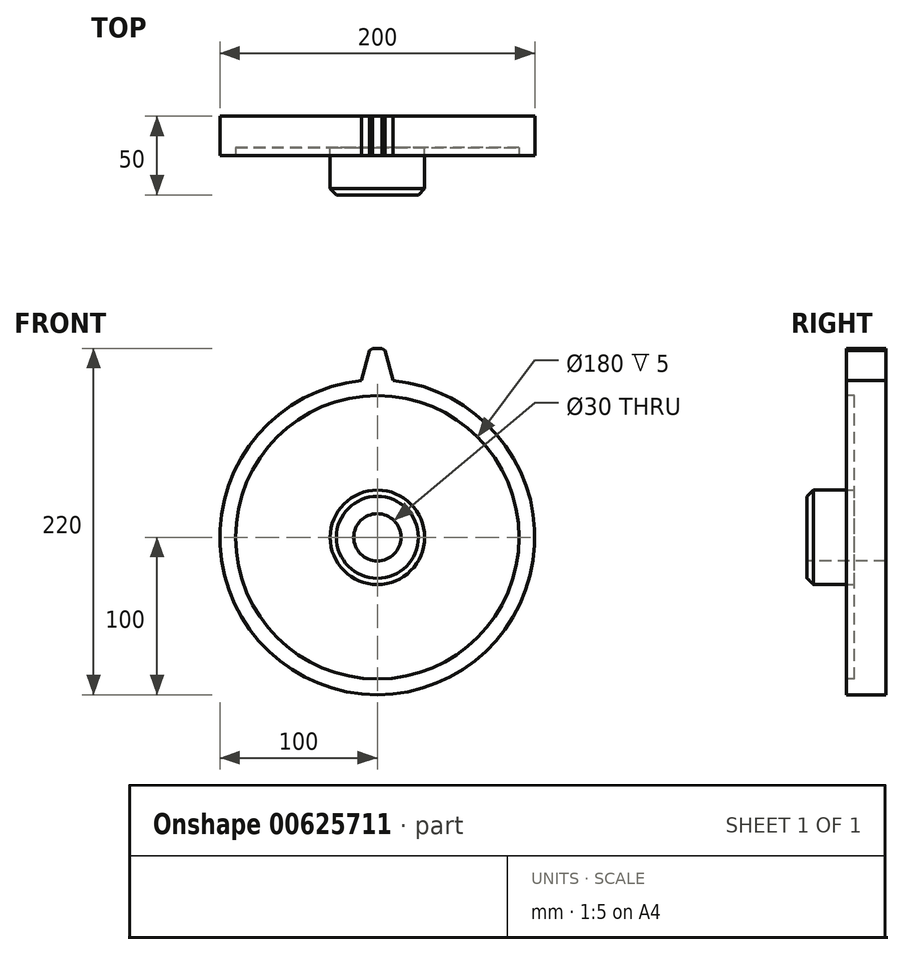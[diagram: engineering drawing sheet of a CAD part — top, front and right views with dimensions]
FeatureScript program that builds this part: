
annotation { "Feature Type Name" : "Feature", "Feature Type Description" : "" }
export const myFeature = defineFeature(function(context is Context, id is Id, definition is map)
    precondition{}
    {
        {
            var Q0;
            Q0=qCreatedBy(makeId("Front.planeOp"),FACE);
            var sketch = newSketch(context, id + "F0", { "sketchPlane" : qUnion([Q0])});
            skCircle(sketch, "E0", {"center": v(0, 0) * mm, "radius": 100 * mm});
            skSolve(sketch);
        }
        {
            var Q0;
            Q0=makeQuery(id+"F0.imprint","IMPRINT",FACE,{"disambiguationData":[TD([[makeQuery(id+"F0.imprint","IMPRINT",EDGE,{"derivedFrom":sQuery(id+"F0.wireOp",EDGE,"E0")}),1.0]])]});
            extrude(context, id + "F1", {"entities" : qUnion([Q0]), "depth" : 25 * mm, "offsetDistance" : 25 * mm});
        }
        {
            var Q0;
            Q0=makeQuery(id+"F1.opExtrude","CAP_FACE",FACE,{"disambiguationData":[OSD([sQuery(id+"F0.wireOp",EDGE,"E0")])],"isStart":false});
            var sketch = newSketch(context, id + "F2", { "sketchPlane" : qUnion([Q0])});
            skLineSegment(sketch, "E1", {"start": v(-10, 99.5) * mm, "end": v(10, 99.5) * mm});
            skLineSegment(sketch, "E2", {"start": v(10, 99.5) * mm, "end": v(4.5, 120) * mm});
            skLineSegment(sketch, "E3", {"start": v(4.5, 120) * mm, "end": v(-4.5, 120) * mm});
            skLineSegment(sketch, "E4", {"start": v(-4.5, 120) * mm, "end": v(-10, 99.5) * mm});
            skSolve(sketch);
        }
        {
            var Q0;
            {var subQ0=sQuery(id+"F2.wireOp",EDGE,"E2");Q0=makeQuery(id+"F2.imprint","IMPRINT",FACE,{"disambiguationData":[TD([[makeQuery(id+"F2.imprint","IMPRINT",EDGE,{"derivedFrom":subQ0}),1.0]])]});}
            var Q1;
            Q1=makeQuery(id+"F1.opExtrude","CAP_FACE",FACE,{"disambiguationData":[OSD([sQuery(id+"F0.wireOp",EDGE,"E0")])],"isStart":true});
            extrude(context, id + "F3", {"entities" : qUnion([Q0]), "operationType" : NewBodyOperationType.ADD, "endBound" : BoundingType.UP_TO_SURFACE, "oppositeDirection" : true, "depth" : 25 * mm, "endBoundEntityFace" : qUnion([Q1]), "offsetDistance" : 25 * mm});
        }
        {
            var Q0;
            Q0=makeQuery(id+"F3.opExtrude","SWEPT_EDGE",EDGE,{"disambiguationData":[OSD([sQuery(id+"F0.wireOp",EDGE,"E0"),sQuery(id+"F2.wireOp",EDGE,"E1"),sQuery(id+"F2.wireOp",EDGE,"E2")])]});
            var Q1;
            Q1=makeQuery(id+"F3.opExtrude","SWEPT_EDGE",EDGE,{"disambiguationData":[OSD([sQuery(id+"F0.wireOp",EDGE,"E0"),sQuery(id+"F2.wireOp",EDGE,"E1"),sQuery(id+"F2.wireOp",EDGE,"E4")])]});
            fillet(context, id + "F4", {"entities" : qUnion([Q0, Q1]), "radius" : 5 * mm, "tangentPropagation" : true, "allowEdgeOverflow" : false});
        }
        {
            var Q0;
            Q0=makeQuery(id+"F3.opExtrude","SWEPT_EDGE",EDGE,{"disambiguationData":[OSD([sQuery(id+"F2.wireOp",EDGE,"E2"),sQuery(id+"F2.wireOp",EDGE,"E3")])]});
            var Q1;
            Q1=makeQuery(id+"F3.opExtrude","SWEPT_EDGE",EDGE,{"disambiguationData":[OSD([sQuery(id+"F2.wireOp",EDGE,"E3"),sQuery(id+"F2.wireOp",EDGE,"E4")])]});
            chamfer(context, id + "F5", {"entities" : qUnion([Q0, Q1]), "width" : 2 * mm, "tangentPropagation" : true});
        }
        {
            var Q0;
            {var subQ0=sQuery(id+"F2.wireOp",EDGE,"E4");var subQ1=sQuery(id+"F2.wireOp",EDGE,"E3");var subQ2=sQuery(id+"F2.wireOp",EDGE,"E2");var subQ3=sQuery(id+"F0.wireOp",EDGE,"E0");Q0=makeQuery(id+"FVngeMlJqadk3JX_1.19.F3.boolean.opBoolean","MERGE",FACE,{"derivedFrom":[makeQuery(id+"FVngeMlJqadk3JX_1.18.F3.boolean.opBoolean","MERGE",FACE,{"derivedFrom":[makeQuery(id+"FVngeMlJqadk3JX_1.17.F3.boolean.opBoolean","MERGE",FACE,{"derivedFrom":[makeQuery(id+"FVngeMlJqadk3JX_1.16.F3.boolean.opBoolean","MERGE",FACE,{"derivedFrom":[makeQuery(id+"FVngeMlJqadk3JX_1.15.F3.boolean.opBoolean","MERGE",FACE,{"derivedFrom":[makeQuery(id+"FVngeMlJqadk3JX_1.14.F3.boolean.opBoolean","MERGE",FACE,{"derivedFrom":[makeQuery(id+"FVngeMlJqadk3JX_1.13.F3.boolean.opBoolean","MERGE",FACE,{"derivedFrom":[makeQuery(id+"FVngeMlJqadk3JX_1.12.F3.boolean.opBoolean","MERGE",FACE,{"derivedFrom":[makeQuery(id+"FVngeMlJqadk3JX_1.11.F3.boolean.opBoolean","MERGE",FACE,{"derivedFrom":[makeQuery(id+"FVngeMlJqadk3JX_1.10.F3.boolean.opBoolean","MERGE",FACE,{"derivedFrom":[makeQuery(id+"FVngeMlJqadk3JX_1.9.F3.boolean.opBoolean","MERGE",FACE,{"derivedFrom":[makeQuery(id+"FVngeMlJqadk3JX_1.8.F3.boolean.opBoolean","MERGE",FACE,{"derivedFrom":[makeQuery(id+"FVngeMlJqadk3JX_1.7.F3.boolean.opBoolean","MERGE",FACE,{"derivedFrom":[makeQuery(id+"FVngeMlJqadk3JX_1.6.F3.boolean.opBoolean","MERGE",FACE,{"derivedFrom":[makeQuery(id+"FVngeMlJqadk3JX_1.5.F3.boolean.opBoolean","MERGE",FACE,{"derivedFrom":[makeQuery(id+"FVngeMlJqadk3JX_1.4.F3.boolean.opBoolean","MERGE",FACE,{"derivedFrom":[makeQuery(id+"FVngeMlJqadk3JX_1.3.F3.boolean.opBoolean","MERGE",FACE,{"derivedFrom":[makeQuery(id+"FVngeMlJqadk3JX_1.2.F3.boolean.opBoolean","MERGE",FACE,{"derivedFrom":[makeQuery(id+"FVngeMlJqadk3JX_1.1.F3.boolean.opBoolean","MERGE",FACE,{"derivedFrom":[makeQuery(id+"F3.boolean.opBoolean","MERGE",FACE,{"derivedFrom":[makeQuery(id+"F1.opExtrude","CAP_FACE",FACE,{"disambiguationData":[OSD([subQ3])],"isStart":false}),makeQuery(id+"F3.opExtrude","CAP_FACE",FACE,{"disambiguationData":[OSD([subQ3,subQ2,subQ1,subQ0])],"isStart":true})]}),makeQuery(id+"FVngeMlJqadk3JX_1.1.F3.opExtrude","CAP_FACE",FACE,{"disambiguationData":[OSD([subQ3,subQ2,subQ1,subQ0])],"isStart":true})]}),makeQuery(id+"FVngeMlJqadk3JX_1.2.F3.opExtrude","CAP_FACE",FACE,{"disambiguationData":[OSD([subQ3,subQ2,subQ1,subQ0])],"isStart":true})]}),makeQuery(id+"FVngeMlJqadk3JX_1.3.F3.opExtrude","CAP_FACE",FACE,{"disambiguationData":[OSD([subQ3,subQ2,subQ1,subQ0])],"isStart":true})]}),makeQuery(id+"FVngeMlJqadk3JX_1.4.F3.opExtrude","CAP_FACE",FACE,{"disambiguationData":[OSD([subQ3,subQ2,subQ1,subQ0])],"isStart":true})]}),makeQuery(id+"FVngeMlJqadk3JX_1.5.F3.opExtrude","CAP_FACE",FACE,{"disambiguationData":[OSD([subQ3,subQ2,subQ1,subQ0])],"isStart":true})]}),makeQuery(id+"FVngeMlJqadk3JX_1.6.F3.opExtrude","CAP_FACE",FACE,{"disambiguationData":[OSD([subQ3,subQ2,subQ1,subQ0])],"isStart":true})]}),makeQuery(id+"FVngeMlJqadk3JX_1.7.F3.opExtrude","CAP_FACE",FACE,{"disambiguationData":[OSD([subQ3,subQ2,subQ1,subQ0])],"isStart":true})]}),makeQuery(id+"FVngeMlJqadk3JX_1.8.F3.opExtrude","CAP_FACE",FACE,{"disambiguationData":[OSD([subQ3,subQ2,subQ1,subQ0])],"isStart":true})]}),makeQuery(id+"FVngeMlJqadk3JX_1.9.F3.opExtrude","CAP_FACE",FACE,{"disambiguationData":[OSD([subQ3,subQ2,subQ1,subQ0])],"isStart":true})]}),makeQuery(id+"FVngeMlJqadk3JX_1.10.F3.opExtrude","CAP_FACE",FACE,{"disambiguationData":[OSD([subQ3,subQ2,subQ1,subQ0])],"isStart":true})]}),makeQuery(id+"FVngeMlJqadk3JX_1.11.F3.opExtrude","CAP_FACE",FACE,{"disambiguationData":[OSD([subQ3,subQ2,subQ1,subQ0])],"isStart":true})]}),makeQuery(id+"FVngeMlJqadk3JX_1.12.F3.opExtrude","CAP_FACE",FACE,{"disambiguationData":[OSD([subQ3,subQ2,subQ1,subQ0])],"isStart":true})]}),makeQuery(id+"FVngeMlJqadk3JX_1.13.F3.opExtrude","CAP_FACE",FACE,{"disambiguationData":[OSD([subQ3,subQ2,subQ1,subQ0])],"isStart":true})]}),makeQuery(id+"FVngeMlJqadk3JX_1.14.F3.opExtrude","CAP_FACE",FACE,{"disambiguationData":[OSD([subQ3,subQ2,subQ1,subQ0])],"isStart":true})]}),makeQuery(id+"FVngeMlJqadk3JX_1.15.F3.opExtrude","CAP_FACE",FACE,{"disambiguationData":[OSD([subQ3,subQ2,subQ1,subQ0])],"isStart":true})]}),makeQuery(id+"FVngeMlJqadk3JX_1.16.F3.opExtrude","CAP_FACE",FACE,{"disambiguationData":[OSD([subQ3,subQ2,subQ1,subQ0])],"isStart":true})]}),makeQuery(id+"FVngeMlJqadk3JX_1.17.F3.opExtrude","CAP_FACE",FACE,{"disambiguationData":[OSD([subQ3,subQ2,subQ1,subQ0])],"isStart":true})]}),makeQuery(id+"FVngeMlJqadk3JX_1.18.F3.opExtrude","CAP_FACE",FACE,{"disambiguationData":[OSD([subQ3,subQ2,subQ1,subQ0])],"isStart":true})]}),makeQuery(id+"FVngeMlJqadk3JX_1.19.F3.opExtrude","CAP_FACE",FACE,{"disambiguationData":[OSD([subQ3,subQ2,subQ1,subQ0])],"isStart":true})]});}
            var sketch = newSketch(context, id + "F6", { "sketchPlane" : qUnion([Q0])});
            skCircle(sketch, "E5", {"center": v(0, 0) * mm, "radius": 90 * mm});
            skSolve(sketch);
        }
        {
            var Q0;
            Q0=makeQuery(id+"F6.imprint","IMPRINT",FACE,{"disambiguationData":[TD([[makeQuery(id+"F6.imprint","IMPRINT",EDGE,{"derivedFrom":sQuery(id+"F6.wireOp",EDGE,"E5")}),1.0]])]});
            var Q1;
            Q1 = qSketchRegion(id + "F8", true);
            extrude(context, id + "F7", {"entities" : qUnion([Q0, Q1]), "operationType" : NewBodyOperationType.REMOVE, "oppositeDirection" : true, "depth" : 5 * mm, "offsetDistance" : 25 * mm});
        }
        {
            var Q0;
            Q0=makeQuery(id+"F7.boolean.opBoolean","COPY",FACE,{"derivedFrom":makeQuery(id+"F7.opExtrude","CAP_FACE",FACE,{"disambiguationData":[OSD([sQuery(id+"F6.wireOp",EDGE,"E5")])],"isStart":false})});
            var sketch = newSketch(context, id + "F8", { "sketchPlane" : qUnion([Q0])});
            skCircle(sketch, "E6", {"center": v(0, 0) * mm, "radius": 30 * mm});
            skSolve(sketch);
        }
        {
            var Q0;
            Q0=makeQuery(id+"F8.imprint","IMPRINT",FACE,{"disambiguationData":[TD([[makeQuery(id+"F8.imprint","IMPRINT",EDGE,{"derivedFrom":sQuery(id+"F8.wireOp",EDGE,"E6")}),1.0]])]});
            extrude(context, id + "F9", {"entities" : qUnion([Q0]), "operationType" : NewBodyOperationType.ADD, "depth" : 30 * mm, "offsetDistance" : 25 * mm});
        }
        {
            var Q0;
            Q0=makeQuery(id+"F9.opExtrude","CAP_FACE",FACE,{"disambiguationData":[OSD([sQuery(id+"F8.wireOp",EDGE,"E6")])],"isStart":false});
            var sketch = newSketch(context, id + "F10", { "sketchPlane" : qUnion([Q0])});
            skCircle(sketch, "E7", {"center": v(0, 0) * mm, "radius": 15 * mm});
            skSolve(sketch);
        }
        {
            var Q0;
            Q0=makeQuery(id+"F10.imprint","IMPRINT",FACE,{"disambiguationData":[TD([[makeQuery(id+"F10.imprint","IMPRINT",EDGE,{"derivedFrom":sQuery(id+"F10.wireOp",EDGE,"E7")}),1.0]])]});
            extrude(context, id + "F11", {"entities" : qUnion([Q0]), "operationType" : NewBodyOperationType.REMOVE, "endBound" : BoundingType.THROUGH_ALL, "oppositeDirection" : true, "depth" : 25 * mm, "offsetDistance" : 25 * mm});
        }
        {
            var Q0;
            Q0=makeQuery(id+"F9.opExtrude","CAP_EDGE",EDGE,{"disambiguationData":[OSD([sQuery(id+"F8.wireOp",EDGE,"E6")])],"isStart":false});
            var Q1;
            Q1=makeQuery(id+"F11.boolean.opBoolean","COPY",EDGE,{"derivedFrom":makeQuery(id+"F11.opExtrude","CAP_EDGE",EDGE,{"disambiguationData":[OSD([sQuery(id+"F10.wireOp",EDGE,"E7")])],"isStart":true})});
            chamfer(context, id + "F12", {"entities" : qUnion([Q0, Q1]), "width" : 4 * mm, "tangentPropagation" : true});
        }
    });
